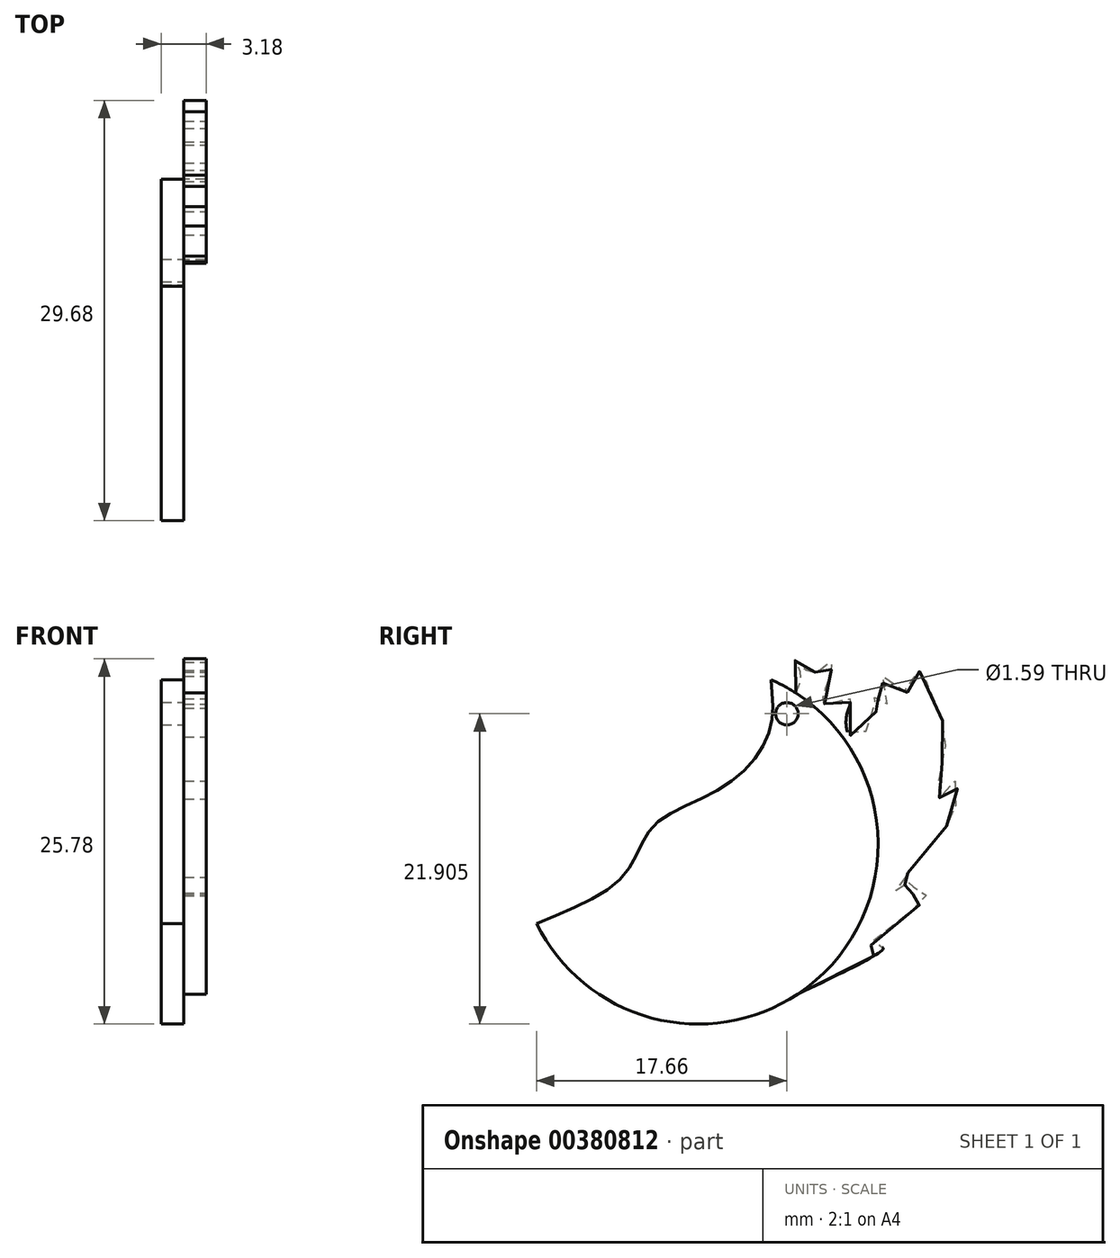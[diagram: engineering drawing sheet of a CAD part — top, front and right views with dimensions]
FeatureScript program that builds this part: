
annotation { "Feature Type Name" : "Feature", "Feature Type Description" : "" }
export const myFeature = defineFeature(function(context is Context, id is Id, definition is map)
    precondition{}
    {
        {
            var Q0;
            Q0=qCreatedBy(makeId("Right.planeOp"),FACE);
            var sketch = newSketch(context, id + "F0", { "sketchPlane" : qUnion([Q0])});
            skArc(sketch, "E0", {"start": v(-11.4, -5.6) * mm, "mid": v(9.16, -8.8) * mm, "end": v(5.14, 11.61) * mm});
            skFitSpline(sketch, "E1", {"points": [v(-11.4, -5.6) * mm, v(-5.17, -2.1) * mm, v(-3.13, 1.3) * mm, v(1.84, 4.09) * mm, v(5, 7.91) * mm, v(5.14, 11.61) * mm], "startDerivative": vector(31.44, 12.73) * mm, "endDerivative": vector(-2.18, 21.56) * mm});
            skSolve(sketch);
        }
        {
            var Q0;
            Q0=makeQuery(id+"F0.imprint","IMPRINT",FACE,{"disambiguationData":[TD([[makeQuery(id+"F0.imprint","IMPRINT",EDGE,{"derivedFrom":sQuery(id+"F0.wireOp",EDGE,"E0")}),1.0]])]});
            extrude(context, id + "F1", {"entities" : qUnion([Q0]), "depth" : 1.59 * mm});
        }
        {
            var Q0;
            Q0=makeQuery(id+"F1.opExtrude","CAP_FACE",FACE,{"disambiguationData":[OSD([sQuery(id+"F0.wireOp",EDGE,"E0"),sQuery(id+"F0.wireOp",EDGE,"E1")])],"isStart":false});
            var sketch = newSketch(context, id + "F2", { "sketchPlane" : qUnion([Q0])});
            skFitSpline(sketch, "E2", {"points": [v(-8.8, -9.15) * mm, v(-5.52, -8.57) * mm, v(-3.61, -6.45) * mm, v(-2.05, -5.57) * mm, v(-1.79, -4.25) * mm, v(-0.38, -2.54) * mm, v(-0.35, -2.63) * mm, v(-0.5, -4.04) * mm, v(0.53, -5.69) * mm, v(1.03, -7.07) * mm, v(2.15, -5.45) * mm, v(1.27, -4.22) * mm, v(1.3, -2.8) * mm, v(0.7, -1.28) * mm, v(1.42, -1.4) * mm, v(2.56, -2.84) * mm, v(3.56, -2.07) * mm, v(2.95, -0.66) * mm, v(3.47, 0.84) * mm, v(3, 2.6) * mm, v(3.92, 2.08) * mm, v(4.39, 3.02) * mm, v(5.6, 2.52) * mm, v(5.2, 5.08) * mm, v(5.97, 4.34) * mm, v(6.7, 6.63) * mm, v(7.77, 8.7) * mm, v(6.83, 10.25) * mm, v(7.27, 11.9) * mm, v(6.77, 13.08) * mm, v(8.1, 12.14) * mm, v(9.3, 12.83) * mm, v(9.3, 11.9) * mm, v(8.9, 9.92) * mm, v(10.68, 10.26) * mm, v(10.48, 9.07) * mm, v(10.92, 7.6) * mm, v(12.56, 9.32) * mm, v(12.2, 10.66) * mm, v(13.3, 9.62) * mm, v(13.05, 11.84) * mm, v(14.93, 10.7) * mm, v(15.42, 12.24) * mm, v(17.15, 8.93) * mm, v(17.3, 6.16) * mm, v(16.9, 3.19) * mm, v(18.1, 4.47) * mm, v(18.05, 2.25) * mm, v(16.86, 0.52) * mm, v(13.9, -3.44) * mm, v(15.32, -2.35) * mm, v(15.18, -3.54) * mm, v(16.31, -3.64) * mm, v(12.2, -7.1) * mm, v(13, -7.3) * mm, v(7.03, -10.58) * mm], "startDerivative": vector(150.11, -0.32) * mm, "endDerivative": vector(-277.28, -131.26) * mm});
            skSolve(sketch);
        }
        {
            var Q0;
            Q0 = qSketchRegion(id + "F2", true);
            var Q1;
            {var subQ0=sQuery(id+"F2.wireOp",EDGE,"E2");var subQ1=makeQuery(id+"F1.opExtrude","CAP_EDGE",EDGE,{"disambiguationData":[OSD([sQuery(id+"F0.wireOp",EDGE,"E0")])],"isStart":false});var subQ2=makeQuery(id+"F2.imprint","INTERSECT",VERTEX,{"disambiguationData":[OD(1.0)],"derivedFrom":[subQ1,subQ0]});Q1=makeQuery(id+"F2.imprint","IMPRINT",FACE,{"disambiguationData":[TD([[makeQuery(id+"F2.imprint","IMPRINT",EDGE,{"disambiguationData":[TD([[subQ2,1.0]])],"derivedFrom":subQ0}),-1.0]])]});}
            var Q2;
            {var subQ0=sQuery(id+"F2.wireOp",EDGE,"E2");var subQ1=makeQuery(id+"F1.opExtrude","CAP_EDGE",EDGE,{"disambiguationData":[OSD([sQuery(id+"F0.wireOp",EDGE,"E0")])],"isStart":false});var subQ2=makeQuery(id+"F2.imprint","INTERSECT",VERTEX,{"disambiguationData":[OD(0.0)],"derivedFrom":[subQ1,subQ0]});Q2=makeQuery(id+"F2.imprint","IMPRINT",FACE,{"disambiguationData":[TD([[makeQuery(id+"F2.imprint","IMPRINT",EDGE,{"disambiguationData":[TD([[subQ2,-1.0]])],"derivedFrom":subQ0}),-1.0]])]});}
            extrude(context, id + "F3", {"entities" : qUnion([Q0, Q1, Q2]), "operationType" : NewBodyOperationType.ADD, "depth" : 1.59 * mm});
        }
        {
            var Q0;
            Q0=makeQuery(id+"F1.opExtrude","CAP_FACE",FACE,{"disambiguationData":[OSD([sQuery(id+"F0.wireOp",EDGE,"E0"),sQuery(id+"F0.wireOp",EDGE,"E1")])],"isStart":false});
            var sketch = newSketch(context, id + "F4", { "sketchPlane" : qUnion([Q0])});
            skCircle(sketch, "E3", {"center": v(6.26, 9.2) * mm, "radius": 0.8 * mm});
            skSolve(sketch);
        }
        {
            var Q0;
            Q0 = qSketchRegion(id + "F4", true);
            extrude(context, id + "F5", {"entities" : qUnion([Q0]), "operationType" : NewBodyOperationType.REMOVE, "oppositeDirection" : true, "depth" : 25.4 * mm});
        }
    });
